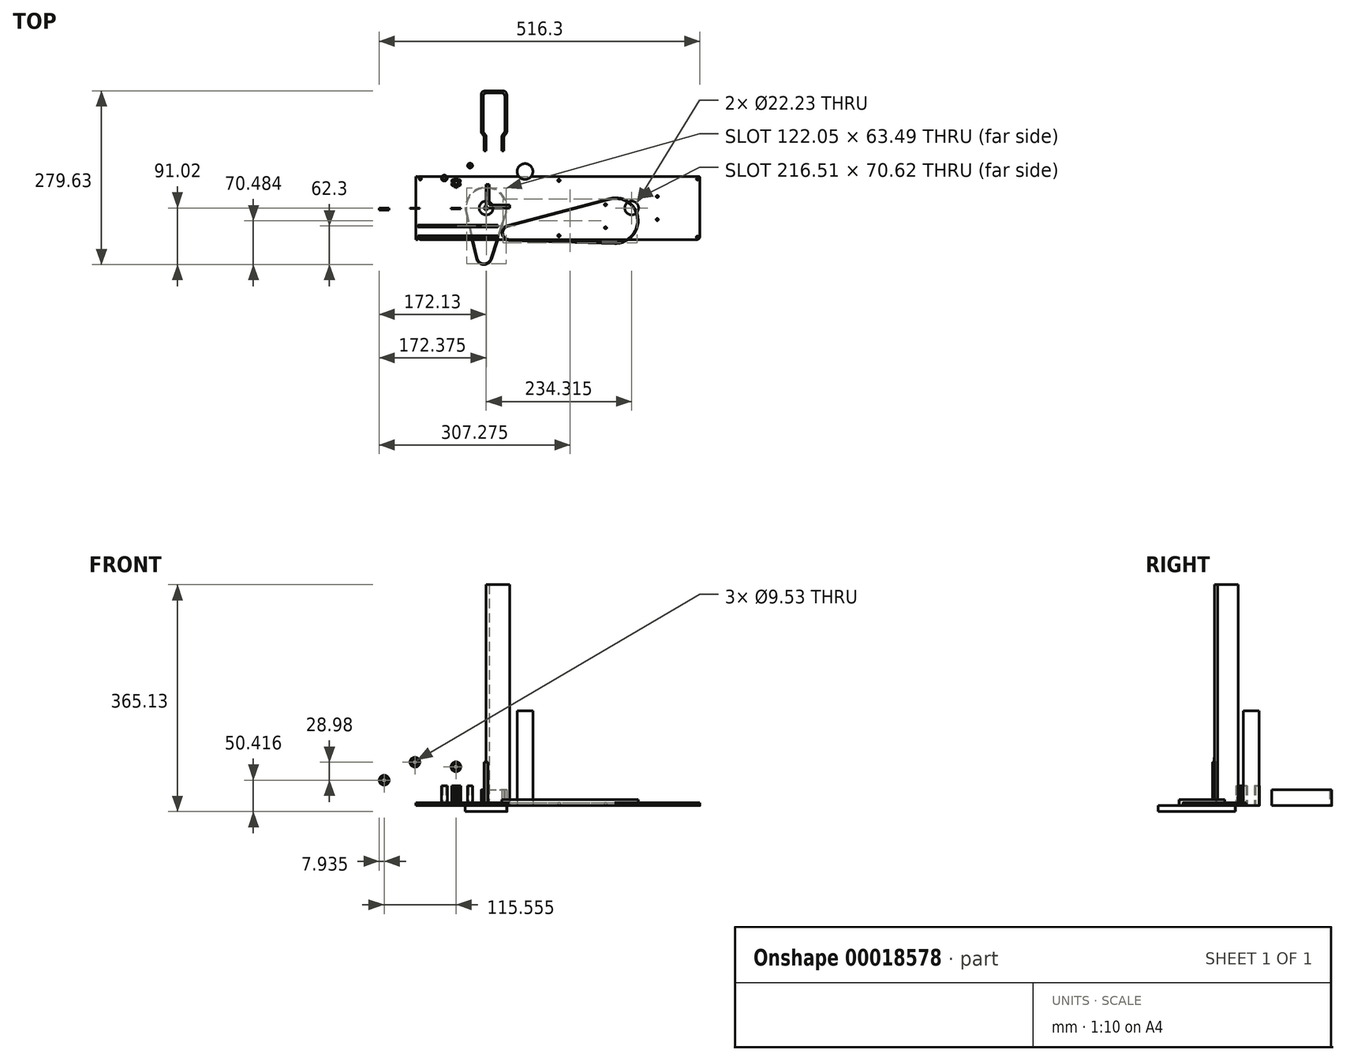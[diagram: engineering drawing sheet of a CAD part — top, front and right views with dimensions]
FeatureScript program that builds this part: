
annotation { "Feature Type Name" : "Feature", "Feature Type Description" : "" }
export const myFeature = defineFeature(function(context is Context, id is Id, definition is map)
    precondition{}
    {
        {
            var Q0;
            Q0=qCreatedBy(makeId("Top.planeOp"),FACE);
            var sketch = newSketch(context, id + "F0", { "sketchPlane" : qUnion([Q0])});
            skCircle(sketch, "E0", {"center": v(0, 0) * mm, "radius": 109.86 * mm, "construction": true});
            skCircle(sketch, "E1", {"center": v(234.32, 0) * mm, "radius": 109.86 * mm, "construction": true});
            skPoint(sketch, "E2.rect.middle", {"position": v(117.16, 38.1) * mm});
            skLineSegment(sketch, "E3", {"start": v(234.32, 0) * mm, "end": v(0, 0) * mm, "construction": true});
            skCircle(sketch, "E4", {"center": v(0, 0) * mm, "radius": 11.11 * mm});
            skLineSegment(sketch, "E5", {"start": v(117.16, 38.1) * mm, "end": v(117.16, 50.8) * mm, "construction": true});
            skCircle(sketch, "E6.MirrorC", {"center": v(234.32, 0) * mm, "radius": 11.11 * mm});
            skLineSegment(sketch, "E7.bottom", {"start": v(-109.85, 50.8) * mm, "end": v(344.17, 50.8) * mm});
            skLineSegment(sketch, "E7.top", {"start": v(-109.85, -50.8) * mm, "end": v(344.17, -50.8) * mm});
            skLineSegment(sketch, "E7.left", {"start": v(-109.86, 50.8) * mm, "end": v(-109.86, -50.8) * mm});
            skLineSegment(sketch, "E7.right", {"start": v(344.17, 50.8) * mm, "end": v(344.17, -50.8) * mm});
            skCircle(sketch, "E8", {"center": v(-105.89, -46.83) * mm, "radius": 1.73 * mm});
            skCircle(sketch, "E9", {"center": v(-105.89, -46.83) * mm, "radius": 3.97 * mm, "construction": true});
            skCircle(sketch, "E10.MirrorC", {"center": v(340.2, -46.83) * mm, "radius": 1.73 * mm});
            skLineSegment(sketch, "E11", {"start": v(-109.86, 0) * mm, "end": v(344.17, 0) * mm, "construction": true});
            skLineSegment(sketch, "E12", {"start": v(0, 50.8) * mm, "end": v(0, -50.8) * mm, "construction": true});
            skLineSegment(sketch, "E13.MirrorCS", {"start": v(234.32, 50.8) * mm, "end": v(234.32, -50.8) * mm, "construction": true});
            skCircle(sketch, "E14", {"center": v(117.16, 44.45) * mm, "radius": 1.9 * mm});
            skCircle(sketch, "E15.MirrorC", {"center": v(117.16, -44.45) * mm, "radius": 1.9 * mm});
            skCircle(sketch, "E16", {"center": v(340.2, 46.83) * mm, "radius": 1.73 * mm});
            skCircle(sketch, "E17.MirrorC", {"center": v(-105.89, 46.83) * mm, "radius": 1.73 * mm});
            skCircle(sketch, "E18", {"center": v(340.2, 46.83) * mm, "radius": 3.97 * mm, "construction": true});
            skLineSegment(sketch, "E19", {"start": v(275.6, 18.54) * mm, "end": v(275.6, -18.54) * mm, "construction": true});
            skPoint(sketch, "E20", {"position": v(275.6, 0) * mm});
            skCircle(sketch, "E21", {"center": v(275.6, 18.54) * mm, "radius": 1.73 * mm});
            skCircle(sketch, "E22.MirrorC", {"center": v(275.6, -18.54) * mm, "radius": 1.73 * mm});
            skLineSegment(sketch, "E23", {"start": v(192.28, 5.33) * mm, "end": v(192.28, -31.75) * mm, "construction": true});
            skLineSegment(sketch, "E24", {"start": v(0, 0) * mm, "end": v(192.28, -13.2) * mm, "construction": true});
            skCircle(sketch, "E25", {"center": v(192.28, 5.33) * mm, "radius": 1.73 * mm});
            skCircle(sketch, "E26", {"center": v(192.28, -31.75) * mm, "radius": 1.73 * mm});
            skSolve(sketch);
        }
        {
            var Q0;
            Q0 = qSketchRegion(id + "F0", true);
            extrude(context, id + "F1", {"entities" : qUnion([Q0]), "depth" : 4.76 * mm});
        }
        {
            var Q0;
            Q0=qCreatedBy(makeId("Top.planeOp"),FACE);
            var sketch = newSketch(context, id + "F2", { "sketchPlane" : qUnion([Q0])});
            skCircle(sketch, "E27", {"center": v(0, 0) * mm, "radius": 3.17 * mm});
            skSolve(sketch);
        }
        {
            var Q0;
            Q0 = qSketchRegion(id + "F2", true);
            extrude(context, id + "F3", {"entities" : qUnion([Q0]), "depth" : 69.85 * mm});
        }
        {
            var Q0;
            Q0=qCreatedBy(makeId("Top.planeOp"),FACE);
            var sketch = newSketch(context, id + "F4", { "sketchPlane" : qUnion([Q0])});
            skCircle(sketch, "E28.cCircle", {"center": v(-48.3, 40.66) * mm, "radius": 6.35 * mm, "construction": true});
            skLineSegment(sketch, "E28.0", {"start": v(-51.96, 47.01) * mm, "end": v(-44.63, 47.01) * mm});
            skLineSegment(sketch, "E28.1", {"start": v(-44.63, 47.01) * mm, "end": v(-40.97, 40.66) * mm});
            skLineSegment(sketch, "E28.2", {"start": v(-40.97, 40.66) * mm, "end": v(-44.63, 34.31) * mm});
            skLineSegment(sketch, "E28.3", {"start": v(-44.63, 34.31) * mm, "end": v(-51.96, 34.31) * mm});
            skLineSegment(sketch, "E28.4", {"start": v(-51.96, 34.31) * mm, "end": v(-55.63, 40.66) * mm});
            skLineSegment(sketch, "E28.5", {"start": v(-55.63, 40.66) * mm, "end": v(-51.96, 47.01) * mm});
            skPoint(sketch, "E28.0.midPoint", {"position": v(-48.3, 47.01) * mm});
            skCircle(sketch, "E29", {"center": v(-48.3, 40.66) * mm, "radius": 2.86 * mm});
            skSolve(sketch);
        }
        {
            var Q0;
            Q0 = qSketchRegion(id + "F4", true);
            extrude(context, id + "F5", {"entities" : qUnion([Q0]), "depth" : 31.75 * mm});
        }
        {
            var Q0;
            Q0=makeQuery(id+"F1.opExtrude","SWEPT_EDGE",EDGE,{"disambiguationData":[OSD([sQuery(id+"F0.wireOp",EDGE,"E7.top"),sQuery(id+"F0.wireOp",EDGE,"E7.left")])]});
            var Q1;
            Q1=makeQuery(id+"F1.opExtrude","SWEPT_EDGE",EDGE,{"disambiguationData":[OSD([sQuery(id+"F0.wireOp",EDGE,"E7.top"),sQuery(id+"F0.wireOp",EDGE,"E7.right")])]});
            fillet(context, id + "F6", {"entities" : qUnion([Q0, Q1]), "radius" : 4.76 * mm, "tangentPropagation" : true, "allowEdgeOverflow" : false});
        }
        {
            var Q0;
            Q0=qCreatedBy(makeId("Top.planeOp"),FACE);
            var sketch = newSketch(context, id + "F7", { "sketchPlane" : qUnion([Q0])});
            skArc(sketch, "E30", {"start": v(34.94, -29.35) * mm, "mid": v(26.89, -41.16) * mm, "end": v(37.42, -50.83) * mm});
            skArc(sketch, "E31", {"start": v(207.01, -55.85) * mm, "mid": v(243.4, -16.22) * mm, "end": v(198.95, 14.1) * mm});
            skLineSegment(sketch, "E32", {"start": v(37.42, -50.83) * mm, "end": v(207.01, -55.85) * mm});
            skLineSegment(sketch, "E33", {"start": v(198.95, 14.1) * mm, "end": v(34.94, -29.35) * mm});
            skArc(sketch, "E34.0", {"start": v(34.62, -28.13) * mm, "mid": v(25.63, -41.3) * mm, "end": v(37.38, -52.1) * mm});
            skLineSegment(sketch, "E34.1", {"start": v(198.63, 15.33) * mm, "end": v(34.62, -28.13) * mm});
            skArc(sketch, "E34.2", {"start": v(206.97, -57.11) * mm, "mid": v(244.66, -16.07) * mm, "end": v(198.63, 15.33) * mm});
            skLineSegment(sketch, "E34.3", {"start": v(37.38, -52.1) * mm, "end": v(206.97, -57.11) * mm});
            skLineSegment(sketch, "E35.0", {"start": v(339.4, -57.15) * mm, "end": v(-105.1, -57.15) * mm});
            skArc(sketch, "E35.1", {"start": v(350.52, -46.04) * mm, "mid": v(347.27, -53.9) * mm, "end": v(339.4, -57.15) * mm});
            skLineSegment(sketch, "E35.2", {"start": v(350.52, 57.15) * mm, "end": v(350.52, -46.04) * mm});
            skLineSegment(sketch, "E35.3", {"start": v(-116.2, 57.15) * mm, "end": v(350.52, 57.15) * mm});
            skLineSegment(sketch, "E35.4", {"start": v(-116.2, -46.04) * mm, "end": v(-116.2, 57.15) * mm});
            skArc(sketch, "E35.5", {"start": v(-105.1, -57.15) * mm, "mid": v(-112.95, -53.9) * mm, "end": v(-116.2, -46.04) * mm});
            skSolve(sketch);
        }
        {
            var Q0;
            Q0=makeQuery(id+"F7.imprint","IMPRINT",FACE,{"disambiguationData":[TD([[makeQuery(id+"F7.imprint","IMPRINT",EDGE,{"derivedFrom":sQuery(id+"F7.wireOp",EDGE,"E30")}),-1.0]])]});
            var Q1;
            {var subQ0=sQuery(id+"F7.wireOp",EDGE,"E35.3");var subQ1=sQuery(id+"F7.wireOp",EDGE,"E31");var subQ2=makeQuery(id+"F7.imprint","INTERSECT",VERTEX,{"disambiguationData":[OD(0.0)],"derivedFrom":[subQ1,subQ0]});Q1=makeQuery(id+"F7.imprint","IMPRINT",FACE,{"disambiguationData":[TD([[makeQuery(id+"F7.imprint","IMPRINT",EDGE,{"disambiguationData":[TD([[subQ2,-1.0]])],"derivedFrom":subQ1}),-1.0]])]});}
            var Q2;
            Q2=sQuery(id+"F7.wireOp",EDGE,"E34.0");
            var Q3;
            Q3=sQuery(id+"F7.wireOp",EDGE,"E30");
            var Q4;
            Q4=sQuery(id+"F7.wireOp",EDGE,"E31");
            var Q5;
            Q5=sQuery(id+"F7.wireOp",EDGE,"E32");
            var Q6;
            Q6=sQuery(id+"F7.wireOp",EDGE,"E33");
            var Q7;
            Q7=sQuery(id+"F7.wireOp",EDGE,"E34.1");
            var Q8;
            Q8=sQuery(id+"F7.wireOp",EDGE,"E34.2");
            var Q9;
            Q9=sQuery(id+"F7.wireOp",EDGE,"E34.3");
            extrude(context, id + "F8", {"entities" : qUnion([Q0, Q1]), "surfaceEntities" : qUnion([Q2, Q3, Q4, Q5, Q6, Q7, Q8, Q9]), "depth" : 9.52 * mm});
        }
        {
            var Q0;
            Q0=qCreatedBy(makeId("Top.planeOp"),FACE);
            var sketch = newSketch(context, id + "F9", { "sketchPlane" : qUnion([Q0])});
            skArc(sketch, "E36", {"start": v(30.75, -10) * mm, "mid": v(1.4, 32.3) * mm, "end": v(-31.5, -7.3) * mm});
            skArc(sketch, "E37", {"start": v(-14.41, -81) * mm, "mid": v(-3.88, -89.74) * mm, "end": v(7.37, -81.94) * mm});
            skLineSegment(sketch, "E38", {"start": v(-31.5, -7.3) * mm, "end": v(-14.41, -81) * mm});
            skLineSegment(sketch, "E39", {"start": v(7.37, -81.94) * mm, "end": v(30.75, -10) * mm});
            skPoint(sketch, "E40.orphan", {"position": v(34, 0) * mm});
            skArc(sketch, "E41.0", {"start": v(-15.65, -81.28) * mm, "mid": v(-3.93, -91.01) * mm, "end": v(8.58, -82.33) * mm});
            skLineSegment(sketch, "E41.1", {"start": v(-32.74, -7.59) * mm, "end": v(-15.65, -81.28) * mm});
            skArc(sketch, "E41.2", {"start": v(31.96, -10.39) * mm, "mid": v(1.45, 33.57) * mm, "end": v(-32.74, -7.59) * mm});
            skLineSegment(sketch, "E41.3", {"start": v(8.58, -82.33) * mm, "end": v(31.96, -10.39) * mm});
            skSolve(sketch);
        }
        {
            var Q0;
            Q0 = qSketchRegion(id + "F9", true);
            extrude(context, id + "F10", {"entities" : qUnion([Q0]), "oppositeDirection" : true, "depth" : 9.52 * mm});
        }
        {
            var Q0;
            Q0=qCreatedBy(makeId("Top.planeOp"),FACE);
            var sketch = newSketch(context, id + "F11", { "sketchPlane" : qUnion([Q0])});
            skLineSegment(sketch, "E42", {"start": v(0, 0) * mm, "end": v(0, 38.1) * mm});
            skLineSegment(sketch, "E43", {"start": v(0, 0) * mm, "end": v(38.1, 0) * mm});
            skLineSegment(sketch, "E44.0", {"start": v(4.76, 4.76) * mm, "end": v(4.76, 38.1) * mm});
            skLineSegment(sketch, "E44.1", {"start": v(4.76, 4.76) * mm, "end": v(38.1, 4.76) * mm});
            skLineSegment(sketch, "E45", {"start": v(0, 38.1) * mm, "end": v(4.76, 38.1) * mm});
            skLineSegment(sketch, "E46", {"start": v(38.1, 4.76) * mm, "end": v(38.1, 0) * mm});
            skSolve(sketch);
        }
        {
            var Q0;
            Q0 = qSketchRegion(id + "F11", true);
            extrude(context, id + "F12", {"entities" : qUnion([Q0]), "depth" : 355.6 * mm});
        }
        {
            var Q0;
            Q0=qCreatedBy(makeId("Top.planeOp"),FACE);
            var sketch = newSketch(context, id + "F13", { "sketchPlane" : qUnion([Q0])});
            skCircle(sketch, "E47", {"center": v(62.62, 58.8) * mm, "radius": 12.7 * mm});
            skSolve(sketch);
        }
        {
            var Q0;
            Q0 = qSketchRegion(id + "F13", true);
            extrude(context, id + "F14", {"entities" : qUnion([Q0]), "depth" : 152.4 * mm});
        }
        {
            var Q0;
            Q0=makeQuery(id+"F3.opExtrude","CAP_FACE",FACE,{"disambiguationData":[OSD([sQuery(id+"F2.wireOp",EDGE,"E27")])],"isStart":false});
            var sketch = newSketch(context, id + "F15", { "sketchPlane" : qUnion([Q0])});
            skLineSegment(sketch, "E48.left", {"start": v(-0.8, 3.97) * mm, "end": v(-0.8, 2.38) * mm});
            skLineSegment(sketch, "E48.top", {"start": v(-0.8, 2.38) * mm, "end": v(0.8, 2.38) * mm});
            skLineSegment(sketch, "E49", {"start": v(-0.8, 3.17) * mm, "end": v(0.8, 3.17) * mm, "construction": true});
            skLineSegment(sketch, "E48.right", {"start": v(0.8, 3.97) * mm, "end": v(0.8, 2.38) * mm});
            skLineSegment(sketch, "E48.bottom", {"start": v(-0.8, 3.97) * mm, "end": v(0.8, 3.97) * mm});
            skLineSegment(sketch, "E50", {"start": v(0, 3.97) * mm, "end": v(0, 2.38) * mm, "construction": true});
            skSolve(sketch);
        }
        {
            var Q0;
            Q0 = qSketchRegion(id + "F15", true);
            extrude(context, id + "F16", {"entities" : qUnion([Q0]), "operationType" : NewBodyOperationType.REMOVE, "endBound" : BoundingType.THROUGH_ALL, "oppositeDirection" : true, "depth" : 25.4 * mm});
        }
        {
            var Q0;
            Q0=qCreatedBy(makeId("Front.planeOp"),FACE);
            var sketch = newSketch(context, id + "F17", { "sketchPlane" : qUnion([Q0])});
            skCircle(sketch, "E51", {"center": v(-114.68, 69.87) * mm, "radius": 4.76 * mm});
            skCircle(sketch, "E52", {"center": v(-114.68, 69.87) * mm, "radius": 7.94 * mm});
            skSolve(sketch);
        }
        {
            var Q0;
            Q0 = qSketchRegion(id + "F17", true);
            extrude(context, id + "F18", {"entities" : qUnion([Q0]), "depth" : 0.81 * mm});
        }
        {
            var Q0;
            Q0=qCreatedBy(makeId("Front.planeOp"),FACE);
            var sketch = newSketch(context, id + "F19", { "sketchPlane" : qUnion([Q0])});
            skCircle(sketch, "E53", {"center": v(-48.64, 62.48) * mm, "radius": 4.76 * mm});
            skCircle(sketch, "E54", {"center": v(-48.64, 62.48) * mm, "radius": 7.94 * mm});
            skSolve(sketch);
        }
        {
            var Q0;
            Q0 = qSketchRegion(id + "F19", true);
            extrude(context, id + "F20", {"entities" : qUnion([Q0]), "depth" : 1.57 * mm});
        }
        {
            var Q0;
            Q0=qCreatedBy(makeId("Top.planeOp"),FACE);
            var sketch = newSketch(context, id + "F21", { "sketchPlane" : qUnion([Q0])});
            skCircle(sketch, "E55", {"center": v(-67.32, 48.15) * mm, "radius": 2.54 * mm});
            skCircle(sketch, "E56", {"center": v(-67.32, 48.15) * mm, "radius": 4.76 * mm});
            skSolve(sketch);
        }
        {
            var Q0;
            Q0 = qSketchRegion(id + "F21", true);
            extrude(context, id + "F22", {"entities" : qUnion([Q0]), "depth" : 31.75 * mm});
        }
        {
            var Q0;
            Q0=qCreatedBy(makeId("Top.planeOp"),FACE);
            var sketch = newSketch(context, id + "F23", { "sketchPlane" : qUnion([Q0])});
            skLineSegment(sketch, "E57", {"start": v(0, 91.77) * mm, "end": v(0, 114.54) * mm});
            skLineSegment(sketch, "E58", {"start": v(-1.86, 119.03) * mm, "end": v(-2.9, 120.07) * mm});
            skLineSegment(sketch, "E59", {"start": v(-4.76, 124.56) * mm, "end": v(-4.76, 179.08) * mm});
            skLineSegment(sketch, "E60", {"start": v(12.7, 98.44) * mm, "end": v(12.7, 172.7) * mm, "construction": true});
            skLineSegment(sketch, "E61.MirrorCS", {"start": v(25.4, 91.77) * mm, "end": v(25.4, 114.54) * mm});
            skLineSegment(sketch, "E62.MirrorCS", {"start": v(30.16, 124.56) * mm, "end": v(30.16, 179.08) * mm});
            skLineSegment(sketch, "E63.MirrorCS", {"start": v(27.26, 119.03) * mm, "end": v(28.3, 120.07) * mm});
            skLineSegment(sketch, "E64", {"start": v(1.59, 185.43) * mm, "end": v(23.81, 185.43) * mm});
            skLineSegment(sketch, "E65.0", {"start": v(28.57, 91.77) * mm, "end": v(28.57, 113.22) * mm});
            skLineSegment(sketch, "E65.1", {"start": v(30.43, 117.71) * mm, "end": v(31.48, 118.76) * mm});
            skLineSegment(sketch, "E65.2", {"start": v(33.34, 123.25) * mm, "end": v(33.34, 182.26) * mm});
            skLineSegment(sketch, "E65.3", {"start": v(-1.59, 188.6) * mm, "end": v(26.99, 188.6) * mm});
            skLineSegment(sketch, "E65.4", {"start": v(-7.94, 124.3) * mm, "end": v(-7.94, 182.26) * mm});
            skLineSegment(sketch, "E65.5", {"start": v(-5.03, 117.71) * mm, "end": v(-5.33, 118.01) * mm});
            skLineSegment(sketch, "E65.6", {"start": v(-3.18, 91.77) * mm, "end": v(-3.18, 113.22) * mm});
            skLineSegment(sketch, "E66", {"start": v(-3.18, 91.77) * mm, "end": v(0, 91.77) * mm});
            skLineSegment(sketch, "E67", {"start": v(25.4, 91.77) * mm, "end": v(28.57, 91.77) * mm});
            skPoint(sketch, "E68.visualSharp", {"position": v(-3.18, 115.85) * mm});
            skArc(sketch, "E68.filletArc", {"start": v(-3.17, 113.22) * mm, "mid": v(-3.66, 115.65) * mm, "end": v(-5.03, 117.71) * mm});
            skPoint(sketch, "E69.visualSharp", {"position": v(0, 117.17) * mm});
            skArc(sketch, "E69.filletArc", {"start": v(0, 114.54) * mm, "mid": v(-0.48, 116.97) * mm, "end": v(-1.86, 119.03) * mm});
            skPoint(sketch, "E70.visualSharp", {"position": v(-7.94, 120.62) * mm});
            skArc(sketch, "E70.filletArc", {"start": v(-7.94, 124.3) * mm, "mid": v(-7.26, 120.9) * mm, "end": v(-5.33, 118.01) * mm});
            skPoint(sketch, "E71.visualSharp", {"position": v(-4.76, 121.93) * mm});
            skArc(sketch, "E71.filletArc", {"start": v(-4.76, 124.56) * mm, "mid": v(-4.28, 122.13) * mm, "end": v(-2.9, 120.07) * mm});
            skPoint(sketch, "E72.visualSharp", {"position": v(-4.76, 185.43) * mm});
            skArc(sketch, "E72.filletArc", {"start": v(1.59, 185.43) * mm, "mid": v(-2.9, 183.57) * mm, "end": v(-4.76, 179.08) * mm});
            skPoint(sketch, "E73.visualSharp", {"position": v(-7.94, 188.6) * mm});
            skArc(sketch, "E73.filletArc", {"start": v(-1.59, 188.6) * mm, "mid": v(-6.08, 186.75) * mm, "end": v(-7.94, 182.26) * mm});
            skPoint(sketch, "E74.visualSharp", {"position": v(30.16, 185.43) * mm});
            skArc(sketch, "E74.filletArc", {"start": v(30.16, 179.08) * mm, "mid": v(28.3, 183.57) * mm, "end": v(23.81, 185.43) * mm});
            skPoint(sketch, "E75.visualSharp", {"position": v(33.34, 188.6) * mm});
            skArc(sketch, "E75.filletArc", {"start": v(33.34, 182.26) * mm, "mid": v(31.48, 186.75) * mm, "end": v(26.99, 188.6) * mm});
            skPoint(sketch, "E76.visualSharp", {"position": v(33.34, 120.62) * mm});
            skArc(sketch, "E76.filletArc", {"start": v(31.48, 118.76) * mm, "mid": v(32.85, 120.82) * mm, "end": v(33.34, 123.25) * mm});
            skPoint(sketch, "E77.visualSharp", {"position": v(30.16, 121.93) * mm});
            skArc(sketch, "E77.filletArc", {"start": v(28.3, 120.07) * mm, "mid": v(29.68, 122.13) * mm, "end": v(30.16, 124.56) * mm});
            skPoint(sketch, "E78.visualSharp", {"position": v(25.4, 117.17) * mm});
            skArc(sketch, "E78.filletArc", {"start": v(27.26, 119.03) * mm, "mid": v(25.88, 116.97) * mm, "end": v(25.4, 114.54) * mm});
            skPoint(sketch, "E79.visualSharp", {"position": v(28.57, 115.85) * mm});
            skArc(sketch, "E79.filletArc", {"start": v(30.43, 117.71) * mm, "mid": v(29.06, 115.65) * mm, "end": v(28.57, 113.22) * mm});
            skSolve(sketch);
        }
        {
            var Q0;
            Q0 = qSketchRegion(id + "F23", true);
            extrude(context, id + "F24", {"entities" : qUnion([Q0]), "depth" : 25.4 * mm});
        }
        {
            var Q0;
            Q0=qCreatedBy(makeId("Top.planeOp"),FACE);
            var sketch = newSketch(context, id + "F25", { "sketchPlane" : qUnion([Q0])});
            skCircle(sketch, "E80", {"center": v(-25.84, 68.24) * mm, "radius": 3.97 * mm});
            skCircle(sketch, "E81", {"center": v(-25.84, 68.24) * mm, "radius": 2.16 * mm});
            skSolve(sketch);
        }
        {
            var Q0;
            Q0 = qSketchRegion(id + "F25", true);
            extrude(context, id + "F26", {"entities" : qUnion([Q0]), "depth" : 31.75 * mm});
        }
        {
            var Q0;
            Q0=makeQuery(id+"F1.opExtrude","SWEPT_EDGE",EDGE,{"disambiguationData":[OSD([sQuery(id+"F0.wireOp",EDGE,"E7.bottom"),sQuery(id+"F0.wireOp",EDGE,"E7.left")])]});
            var Q1;
            Q1=makeQuery(id+"F1.opExtrude","SWEPT_EDGE",EDGE,{"disambiguationData":[OSD([sQuery(id+"F0.wireOp",EDGE,"E7.bottom"),sQuery(id+"F0.wireOp",EDGE,"E7.right")])]});
            fillet(context, id + "F27", {"entities" : qUnion([Q0, Q1]), "radius" : 2.38 * mm, "tangentPropagation" : true, "allowEdgeOverflow" : false});
        }
        {
            var Q0;
            Q0=qCreatedBy(makeId("Top.planeOp"),FACE);
            var sketch = newSketch(context, id + "F28", { "sketchPlane" : qUnion([Q0])});
            skLineSegment(sketch, "E82", {"start": v(0, -25.12) * mm, "end": v(0, -50.52) * mm});
            skLineSegment(sketch, "E83", {"start": v(0, -50.52) * mm, "end": v(22.23, -63.35) * mm});
            skLineSegment(sketch, "E84", {"start": v(22.23, -63.35) * mm, "end": v(22.23, -82.4) * mm});
            skLineSegment(sketch, "E85.0", {"start": v(19.05, -65.18) * mm, "end": v(19.05, -82.4) * mm});
            skLineSegment(sketch, "E85.1", {"start": v(-3.17, -52.35) * mm, "end": v(19.05, -65.18) * mm});
            skLineSegment(sketch, "E85.2", {"start": v(-3.17, -25.12) * mm, "end": v(-3.17, -52.35) * mm});
            skLineSegment(sketch, "E86", {"start": v(0, -25.12) * mm, "end": v(-3.17, -25.12) * mm});
            skLineSegment(sketch, "E87", {"start": v(19.05, -82.4) * mm, "end": v(22.23, -82.4) * mm});
            skSolve(sketch);
        }
        {
            var Q0;
            Q0 = qSketchRegion(id + "F28", true);
            extrude(context, id + "F29", {"entities" : qUnion([Q0]), "depth" : 9.52 * mm});
        }
        {
            var Q0;
            Q0=makeQuery(id+"F29.opExtrude","SWEPT_FACE",FACE,{"disambiguationData":[OSD([sQuery(id+"F28.wireOp",EDGE,"E85.0")])]});
            var sketch = newSketch(context, id + "F30", { "sketchPlane" : qUnion([Q0])});
            skLineSegment(sketch, "E88", {"start": v(37.82, 9.53) * mm, "end": v(37.82, 0) * mm, "construction": true});
            skCircle(sketch, "E89", {"center": v(46.55, 3.97) * mm, "radius": 1.97 * mm});
            skCircle(sketch, "E90.MirrorC", {"center": v(29.09, 3.97) * mm, "radius": 1.97 * mm});
            skSolve(sketch);
        }
        {
            var Q0;
            Q0 = qSketchRegion(id + "F30", true);
            extrude(context, id + "F31", {"entities" : qUnion([Q0]), "operationType" : NewBodyOperationType.REMOVE, "endBound" : BoundingType.THROUGH_ALL, "depth" : 25.4 * mm});
        }
        {
            var Q0;
            Q0=makeQuery(id+"F5.opExtrude","CAP_FACE",FACE,{"disambiguationData":[OSD([sQuery(id+"F4.wireOp",EDGE,"E28.0"),sQuery(id+"F4.wireOp",EDGE,"E28.1"),sQuery(id+"F4.wireOp",EDGE,"E28.2"),sQuery(id+"F4.wireOp",EDGE,"E28.3"),sQuery(id+"F4.wireOp",EDGE,"E28.4"),sQuery(id+"F4.wireOp",EDGE,"E28.5"),sQuery(id+"F4.wireOp",EDGE,"E29")])],"isStart":false});
            var sketch = newSketch(context, id + "F32", { "sketchPlane" : qUnion([Q0])});
            skCircle(sketch, "E91", {"center": v(-48.3, 47.01) * mm, "radius": 1.59 * mm});
            skPoint(sketch, "E92", {"position": v(-48.3, 40.66) * mm});
            skCircle(sketch, "E93.1.1", {"center": v(-53.8, 43.84) * mm, "radius": 1.59 * mm});
            skCircle(sketch, "E93.2.1", {"center": v(-53.8, 37.49) * mm, "radius": 1.59 * mm});
            skCircle(sketch, "E93.3.1", {"center": v(-48.3, 34.31) * mm, "radius": 1.59 * mm});
            skCircle(sketch, "E93.4.1", {"center": v(-42.8, 37.49) * mm, "radius": 1.59 * mm});
            skCircle(sketch, "E93.5.1", {"center": v(-42.8, 43.84) * mm, "radius": 1.59 * mm});
            skSolve(sketch);
        }
        {
            var Q0;
            Q0 = qSketchRegion(id + "F32", true);
            extrude(context, id + "F33", {"entities" : qUnion([Q0]), "operationType" : NewBodyOperationType.REMOVE, "endBound" : BoundingType.THROUGH_ALL, "oppositeDirection" : true, "depth" : 25.4 * mm});
        }
        {
            var Q0;
            Q0=qCreatedBy(makeId("Front.planeOp"),FACE);
            var sketch = newSketch(context, id + "F34", { "sketchPlane" : qUnion([Q0])});
            skCircle(sketch, "E94", {"center": v(-164.2, 40.89) * mm, "radius": 4.76 * mm});
            skCircle(sketch, "E95", {"center": v(-164.2, 40.89) * mm, "radius": 7.94 * mm});
            skSolve(sketch);
        }
        {
            var Q0;
            Q0=makeQuery(id+"F34.imprint","IMPRINT",FACE,{"disambiguationData":[TD([[makeQuery(id+"F34.imprint","IMPRINT",EDGE,{"derivedFrom":sQuery(id+"F34.wireOp",EDGE,"E94")}),-1.0]])]});
            var Q1;
            Q1=sQuery(id+"F34.wireOp",EDGE,"E94");
            var Q2;
            Q2=sQuery(id+"F34.wireOp",EDGE,"E95");
            extrude(context, id + "F35", {"entities" : qUnion([Q0]), "surfaceEntities" : qUnion([Q1, Q2]), "depth" : 3.17 * mm});
        }
        {
            var Q0;
            Q0=makeQuery(id+"F1.opExtrude","SWEPT_FACE",FACE,{"disambiguationData":[OSD([sQuery(id+"F0.wireOp",EDGE,"E7.left")])]});
            var sketch = newSketch(context, id + "F36", { "sketchPlane" : qUnion([Q0])});
            skLineSegment(sketch, "E96.bottom", {"start": v(-50.8, 4.76) * mm, "end": v(50.8, 4.76) * mm});
            skLineSegment(sketch, "E96.top", {"start": v(-50.8, 0) * mm, "end": v(50.8, 0) * mm});
            skLineSegment(sketch, "E96.left", {"start": v(50.8, 4.76) * mm, "end": v(50.8, 0) * mm});
            skLineSegment(sketch, "E96.right", {"start": v(-50.8, 4.76) * mm, "end": v(-50.8, 0) * mm});
            skSolve(sketch);
        }
        {
            var Q0;
            Q0 = qSketchRegion(id + "F36", true);
            extrude(context, id + "F37", {"entities" : qUnion([Q0]), "operationType" : NewBodyOperationType.ADD, "depth" : 3.17 * mm});
        }
        {
            var Q0;
            Q0=makeQuery(id+"F29.opExtrude","SWEPT_BODY",BODY,{"disambiguationData":[OSD([sQuery(id+"F28.wireOp",EDGE,"E82"),sQuery(id+"F28.wireOp",EDGE,"E83"),sQuery(id+"F28.wireOp",EDGE,"E84"),sQuery(id+"F28.wireOp",EDGE,"E85.0"),sQuery(id+"F28.wireOp",EDGE,"E85.1"),sQuery(id+"F28.wireOp",EDGE,"E85.2"),sQuery(id+"F28.wireOp",EDGE,"E86"),sQuery(id+"F28.wireOp",EDGE,"E87")])]});
            deleteBodies(context, id + "F38", {"entities" : qUnion([Q0])});
        }
    });
